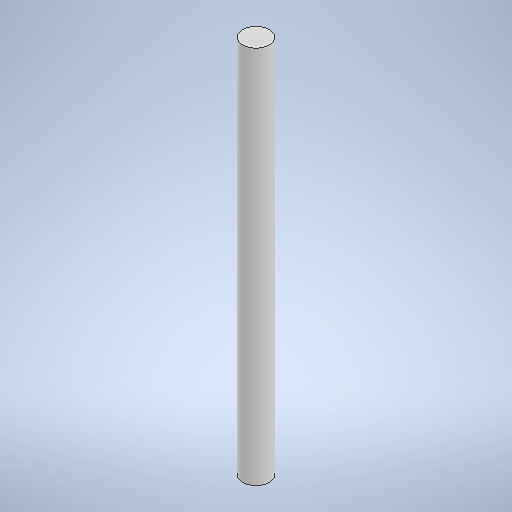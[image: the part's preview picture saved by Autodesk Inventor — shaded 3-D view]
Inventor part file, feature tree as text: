
AUTODESK INVENTOR PART (.ipt)
format: ipt  version: 2025 (Build 290162000, 162)  size: 246,784 bytes
history: native  units: mm
features: other x1, extrude x1, sketch x1
ambient origin geometry x8: Origin, YZ Plane, XZ Plane, XY Plane, X Axis, Y Axis, Z Axis, Center Point
bodies: Body1 (feature_tree)
feature tree (3):
  other  "Bryła1"
  extrude  "Wyciągnięcie proste1"  Depth=8.0mm
  sketch  "Szkic1"
